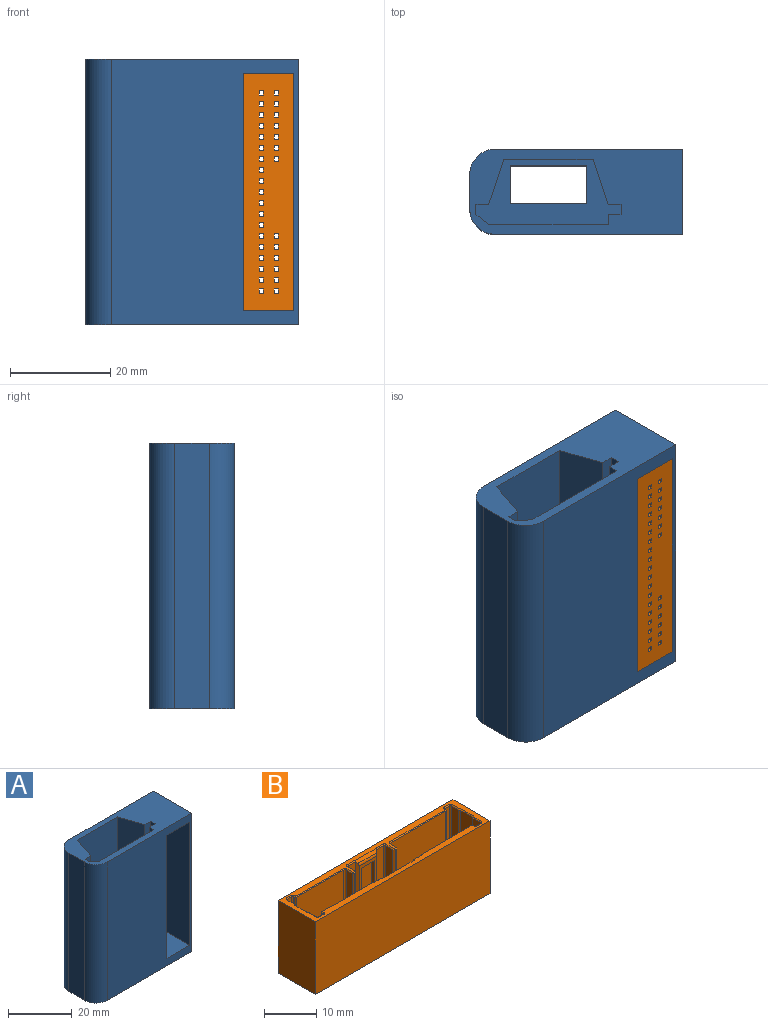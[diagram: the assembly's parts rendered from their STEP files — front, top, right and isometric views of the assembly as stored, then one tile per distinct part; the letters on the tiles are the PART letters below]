
ASSEMBLY  parts=2 mates=1
PART A: 28 faces, bbox 42.5x17x53 mm
  f0: plane 42.5x17mm, normal (0,0,-1), area 597.1mm2, adj f2,f3,f4,f5,f22,f23,f24,f25
  f1: plane 29x13.02mm, normal (0,0,1), area 182.2mm2, adj f11,f12,f13,f14,f15,f16,f17,f18
  f2: plane 53x37.42mm, normal (0,-1,0), area 1511.3mm2, adj f0,f5,f6,f7,f8,f9,f10,f26
  f3: plane 53x37.42mm, normal (0,1,0), area 1511.3mm2, adj f0,f5,f6,f7,f8,f9,f10,f27
  f4: plane 53x6.84mm, normal (-1,0,0), area 362.5mm2, adj f0,f6,f26,f27
  f5: plane 53x17mm, normal (1,0,0), area 901mm2, adj f0,f2,f3,f6
  f6: plane 42.5x17mm, normal (0,0,1), area 414.9mm2, adj f2,f3,f4,f5,f11,f12,f13,f14
  f7: plane 17x10mm, normal (0,0,-1), area 170mm2, adj f2,f3,f8,f10
  f8: plane 47.2x17mm, normal (-1,0,0), area 802.4mm2, adj f2,f3,f7,f9
  f9: plane 17x10mm, normal (0,0,1), area 170mm2, adj f2,f3,f8,f10
  f10: plane 47.2x17mm, normal (1,0,0), area 802.4mm2, adj f2,f3,f7,f9
  f11: plane 51.5x2mm, normal (1,0,0), area 103mm2, adj f1,f6,f12,f21
  f12: plane 51.5x2.54mm, normal (0.62,0.79,0), area 166.5mm2, adj f1,f6,f11,f13
  f13: plane 51.5x23.92mm, normal (0,1,0), area 1231.9mm2, adj f1,f6,f12,f14
  f14: plane 51.5x2mm, normal (-1,0,0), area 103mm2, adj f1,f6,f13,f15
  f15: plane 51.5x2.54mm, normal (0,1,0), area 130.8mm2, adj f1,f6,f14,f16
  f16: plane 51.5x2mm, normal (-1,0,0), area 103mm2, adj f1,f6,f15,f17
  f17: plane 51.5x2.54mm, normal (0,-1,0), area 130.8mm2, adj f1,f6,f16,f18
  f18: plane 51.5x9.02mm, normal (-0.95,-0.32,0), area 490.5mm2, adj f1,f6,f17,f19
  f19: plane 51.5x17.8mm, normal (0,-1,0), area 916.7mm2, adj f1,f6,f18,f20
  f20: plane 51.5x9.02mm, normal (0.95,-0.32,0), area 490.5mm2, adj f1,f6,f19,f21
  f21: plane 51.5x2.54mm, normal (0,-1,0), area 130.8mm2, adj f1,f6,f11,f20
  f22: plane 15.25x1.5mm, normal (0,-1,0), area 22.9mm2, adj f0,f1,f23,f25
  f23: plane 7.5x1.5mm, normal (1,0,0), area 11.3mm2, adj f0,f1,f22,f24
  f24: plane 15.25x1.5mm, normal (0,1,0), area 22.9mm2, adj f0,f1,f23,f25
  f25: plane 7.5x1.5mm, normal (-1,0,0), area 11.3mm2, adj f0,f1,f22,f24
  f26: cylinder r=5.08mm len=53mm, axis (0,0,-1), area 422.9mm2, adj f0,f2,f4,f6
  f27: cylinder r=5.08mm len=53mm, axis (0,0,1), area 422.9mm2, adj f0,f3,f4,f6
PART B: 258 faces, bbox 47.3x10.1x17.1 mm
  f0: plane 47.2x10mm, normal (0,0,-1), area 448.9mm2, adj f3,f4,f128,f129,f130,f131,f132,f133
  f1: plane 44.6x8.4mm, normal (0,0,1), area 288.9mm2, adj f9,f10,f22,f23,f34,f35,f39,f40
  f2: plane 47.2x10mm, normal (0,0,1), area 137.9mm2, adj f3,f4,f5,f6,f7,f8,f11,f12
  f3: plane 47.2x17mm, normal (0,-1,0), area 802.4mm2, adj f0,f2,f4,f128
  f4: plane 17x10mm, normal (1,0,0), area 170mm2, adj f0,f2,f3,f129
  f5: plane 2x0.2mm, normal (0,-0.71,0.71), area 0.5mm2, adj f2,f6,f81,f82
  f6: cone r=0.3mm half-angle=45deg, axis (0,0,1), area 0.1mm2, adj f2,f5,f7,f83
  f7: plane 2.1x0.2mm, normal (-0.71,0,0.71), area 0.6mm2, adj f2,f6,f8,f84
  f8: plane 0.38x0.38mm, normal (-0.5,-0.5,0.71), area 0.1mm2, adj f2,f7,f9,f11
  f9: plane 13.8x0.3mm, normal (-0.71,-0.71,0), area 5.9mm2, adj f1,f8,f10,f84
  f10: plane 13.8x0.4mm, normal (0,-1,0), area 5.5mm2, adj f1,f9,f11,f93
  f11: plane 0.4x0.2mm, normal (0,-0.71,0.71), area 0.1mm2, adj f2,f8,f10,f12
  f12: plane 0.38x0.38mm, normal (0.5,-0.5,0.71), area 0.1mm2, adj f2,f11,f13,f93
  f13: plane 1.6x0.2mm, normal (0.71,0,0.71), area 0.4mm2, adj f2,f12,f14,f94
  f14: cone r=0.4mm half-angle=45deg, axis (0,0,1), area 0.2mm2, adj f2,f13,f15,f95
  f15: plane 14.9x0.2mm, normal (0,-0.71,0.71), area 4.2mm2, adj f2,f14,f16,f96
  f16: cone r=0.2mm half-angle=45deg, axis (0,0,-1), area 0.1mm2, adj f2,f15,f17,f97
  f17: plane 0.2x0.2mm, normal (0.71,0,0.71), area 0.1mm2, adj f2,f16,f18,f98
  f18: cone r=0.4mm half-angle=45deg, axis (0,0,1), area 0.2mm2, adj f2,f17,f19,f99
  f19: plane 1.1x0.2mm, normal (0,-0.71,0.71), area 0.3mm2, adj f2,f18,f20,f100
  f20: cone r=0.4mm half-angle=45deg, axis (0,0,1), area 0.2mm2, adj f2,f19,f21,f101
  f21: plane 2x0.2mm, normal (-0.71,0,0.71), area 0.6mm2, adj f2,f20,f22,f24
  f22: plane 13.8x2mm, normal (-1,0,0), area 27.6mm2, adj f1,f21,f23,f101
  f23: plane 13.8x0.35mm, normal (-0.87,-0.5,0), area 5.5mm2, adj f1,f22,f24,f102
  f24: plane 0.4x0.4mm, normal (-0.61,-0.35,0.71), area 0.1mm2, adj f2,f21,f23,f25
  f25: plane 3.21x0.2mm, normal (-0.71,0,0.71), area 0.9mm2, adj f2,f24,f26,f102
  f26: plane 0.4x0.4mm, normal (-0.61,0.35,0.71), area 0.1mm2, adj f2,f25,f27,f103
  f27: plane 2x0.2mm, normal (-0.71,0,0.71), area 0.6mm2, adj f2,f26,f28,f104
  f28: cone r=0.4mm half-angle=45deg, axis (0,0,1), area 0.2mm2, adj f2,f27,f29,f105
  f29: plane 1.1x0.2mm, normal (0,0.71,0.71), area 0.3mm2, adj f2,f28,f30,f106
  f30: cone r=0.4mm half-angle=45deg, axis (0,0,1), area 0.2mm2, adj f2,f29,f31,f107
  f31: plane 0.2x0.2mm, normal (0.71,0,0.71), area 0.1mm2, adj f2,f30,f32,f108
  f32: cone r=0.2mm half-angle=45deg, axis (0,0,-1), area 0.1mm2, adj f2,f31,f33,f109
  f33: plane 13.5x0.2mm, normal (0,0.71,0.71), area 3.8mm2, adj f2,f32,f34,f36
  f34: plane 13.8x13.5mm, normal (0,1,0), area 186.3mm2, adj f1,f33,f35,f109
  f35: plane 13.8x0.35mm, normal (-0.5,0.87,0), area 5.5mm2, adj f1,f34,f36,f110
  f36: plane 0.4x0.4mm, normal (-0.35,0.61,0.71), area 0.1mm2, adj f2,f33,f35,f37
  f37: plane 1.91x0.2mm, normal (0,0.71,0.71), area 0.5mm2, adj f2,f36,f38,f110
  f38: plane 0.4x0.4mm, normal (-0.35,0.61,0.71), area 0.1mm2, adj f2,f37,f39,f41
  f39: plane 13.8x0.35mm, normal (-0.5,0.87,0), area 5.5mm2, adj f1,f38,f40,f110
  f40: plane 13.8x8.11mm, normal (0,1,0), area 111.9mm2, adj f1,f39,f41,f111
  f41: plane 8.21x0.2mm, normal (0,0.71,0.71), area 2.3mm2, adj f2,f38,f40,f42
  f42: plane 0.4x0.4mm, normal (0.35,0.61,0.71), area 0.1mm2, adj f2,f41,f43,f111
  f43: plane 1.91x0.2mm, normal (0,0.71,0.71), area 0.5mm2, adj f2,f42,f44,f112
  f44: plane 0.4x0.4mm, normal (0.35,0.61,0.71), area 0.1mm2, adj f2,f43,f45,f47
  f45: plane 13.8x0.35mm, normal (0.5,0.87,0), area 5.5mm2, adj f1,f44,f46,f112
  f46: plane 13.8x13.5mm, normal (0,1,0), area 186.3mm2, adj f1,f45,f47,f113
  f47: plane 13.5x0.2mm, normal (0,0.71,0.71), area 3.8mm2, adj f2,f44,f46,f48
  f48: cone r=0.2mm half-angle=45deg, axis (0,0,-1), area 0.1mm2, adj f2,f47,f49,f113
  f49: plane 0.2x0.2mm, normal (-0.71,0,0.71), area 0.1mm2, adj f2,f48,f50,f114
  f50: cone r=0.4mm half-angle=45deg, axis (0,0,1), area 0.2mm2, adj f2,f49,f51,f115
  f51: plane 1.1x0.2mm, normal (0,0.71,0.71), area 0.3mm2, adj f2,f50,f52,f116
  f52: cone r=0.4mm half-angle=45deg, axis (0,0,1), area 0.2mm2, adj f2,f51,f53,f117
  f53: plane 2x0.2mm, normal (0.71,0,0.71), area 0.6mm2, adj f2,f52,f54,f56
  f54: plane 13.8x2mm, normal (1,0,0), area 27.6mm2, adj f1,f53,f55,f117
  f55: plane 13.8x0.35mm, normal (0.87,0.5,0), area 5.5mm2, adj f1,f54,f56,f118
  f56: plane 0.4x0.4mm, normal (0.61,0.35,0.71), area 0.1mm2, adj f2,f53,f55,f57
  f57: plane 3.21x0.2mm, normal (0.71,0,0.71), area 0.9mm2, adj f2,f56,f58,f118
  f58: plane 0.4x0.4mm, normal (0.61,-0.35,0.71), area 0.1mm2, adj f2,f57,f59,f119
  f59: plane 2x0.2mm, normal (0.71,0,0.71), area 0.6mm2, adj f2,f58,f60,f120
  f60: cone r=0.4mm half-angle=45deg, axis (0,0,1), area 0.2mm2, adj f2,f59,f61,f121
  f61: plane 1.1x0.2mm, normal (0,-0.71,0.71), area 0.3mm2, adj f2,f60,f62,f122
  f62: cone r=0.4mm half-angle=45deg, axis (0,0,1), area 0.2mm2, adj f2,f61,f63,f123
  f63: plane 0.2x0.2mm, normal (-0.71,0,0.71), area 0.1mm2, adj f2,f62,f64,f124
  f64: cone r=0.2mm half-angle=45deg, axis (0,0,-1), area 0.1mm2, adj f2,f63,f65,f125
  f65: plane 12.7x0.2mm, normal (0,-0.71,0.71), area 3.6mm2, adj f2,f64,f66,f126
  f66: cone r=0.4mm half-angle=45deg, axis (0,0,1), area 0.2mm2, adj f2,f65,f67,f127
  f67: plane 1.6x0.2mm, normal (-0.71,0,0.71), area 0.4mm2, adj f2,f66,f68,f70
  f68: plane 13.8x1.6mm, normal (-1,0,0), area 22.1mm2, adj f1,f67,f69,f127
  f69: plane 13.8x0.3mm, normal (-0.71,-0.71,0), area 5.9mm2, adj f1,f68,f70,f72
  f70: plane 0.38x0.38mm, normal (-0.5,-0.5,0.71), area 0.1mm2, adj f2,f67,f69,f71
  f71: plane 0.4x0.2mm, normal (0,-0.71,0.71), area 0.1mm2, adj f2,f70,f72,f74
  f72: plane 13.8x0.4mm, normal (0,-1,0), area 5.5mm2, adj f1,f69,f71,f73
  f73: plane 13.8x0.3mm, normal (0.71,-0.71,0), area 5.9mm2, adj f1,f72,f74,f86
  f74: plane 0.38x0.38mm, normal (0.5,-0.5,0.71), area 0.1mm2, adj f2,f71,f73,f75
  f75: plane 2.1x0.2mm, normal (0.71,0,0.71), area 0.6mm2, adj f2,f74,f76,f86
  f76: cone r=0.3mm half-angle=45deg, axis (0,0,1), area 0.1mm2, adj f2,f75,f77,f85
  f77: plane 2x0.2mm, normal (0,-0.71,0.71), area 0.5mm2, adj f2,f76,f78,f79
  f78: plane 13.8x2mm, normal (0,-1,0), area 27.6mm2, adj f1,f77,f79,f85
  f79: plane 14.09x0.79mm, normal (-0.71,-0.71,0), area 9.5mm2, adj f1,f2,f77,f78,f80,f87,f92
  f80: plane 5.86x0.64mm, normal (0,-0.82,0.57), area 4.2mm2, adj f2,f79,f81,f92
  f81: plane 14.09x0.79mm, normal (0.71,-0.71,0), area 9.5mm2, adj f1,f2,f5,f80,f82,f87,f92
  f82: plane 13.8x2mm, normal (0,-1,0), area 27.6mm2, adj f1,f5,f81,f83
  f83: cylinder r=0.2mm len=13.8mm, axis (0,0,-1), area 4.3mm2, adj f1,f6,f82,f84
  f84: plane 13.8x2.1mm, normal (-1,0,0), area 29mm2, adj f1,f7,f9,f83
  f85: cylinder r=0.2mm len=13.8mm, axis (0,0,-1), area 4.3mm2, adj f1,f76,f78,f86
  f86: plane 13.8x2.1mm, normal (1,0,0), area 29mm2, adj f1,f73,f75,f85
  f87: plane 12.78x4.6mm, normal (0,-1,0), area 15.6mm2, adj f1,f79,f81,f88,f90,f91,f92
  f88: plane 12.13x0.9mm, normal (-1,0,0), area 10.9mm2, adj f1,f87,f89,f91
  f89: plane 12.13x3.6mm, normal (0,-1,0), area 43.7mm2, adj f1,f88,f90,f91
  f90: plane 12.13x0.9mm, normal (1,0,0), area 10.9mm2, adj f1,f87,f89,f91
  f91: plane 3.6x0.9mm, normal (0,0.14,-0.99), area 3.3mm2, adj f87,f88,f89,f90
  f92: cylinder r=1mm len=4.96mm, axis (1,0,0), area 2.9mm2, adj f79,f80,f81,f87
  f93: plane 13.8x0.3mm, normal (0.71,-0.71,0), area 5.9mm2, adj f1,f10,f12,f94
  f94: plane 13.8x1.6mm, normal (1,0,0), area 22.1mm2, adj f1,f13,f93,f95
  f95: cylinder r=0.3mm len=13.8mm, axis (0,0,1), area 6.5mm2, adj f1,f14,f94,f96
  f96: plane 14.9x13.8mm, normal (0,-1,0), area 205.6mm2, adj f1,f15,f95,f97
  f97: cylinder r=0.3mm len=13.8mm, axis (0,0,1), area 6.5mm2, adj f1,f16,f96,f98
  f98: plane 13.8x0.2mm, normal (1,0,0), area 2.8mm2, adj f1,f17,f97,f99
  f99: cylinder r=0.3mm len=13.8mm, axis (0,0,1), area 6.5mm2, adj f1,f18,f98,f100
  f100: plane 13.8x1.1mm, normal (0,-1,0), area 15.2mm2, adj f1,f19,f99,f101
  f101: cylinder r=0.3mm len=13.8mm, axis (0,0,1), area 6.5mm2, adj f1,f20,f22,f100
  f102: plane 13.8x3.11mm, normal (-1,0,0), area 42.9mm2, adj f1,f23,f25,f103
  f103: plane 13.8x0.35mm, normal (-0.87,0.5,0), area 5.5mm2, adj f1,f26,f102,f104
  f104: plane 13.8x2mm, normal (-1,0,0), area 27.6mm2, adj f1,f27,f103,f105
  f105: cylinder r=0.3mm len=13.8mm, axis (0,0,1), area 6.5mm2, adj f1,f28,f104,f106
  f106: plane 13.8x1.1mm, normal (0,1,0), area 15.2mm2, adj f1,f29,f105,f107
  f107: cylinder r=0.3mm len=13.8mm, axis (0,0,1), area 6.5mm2, adj f1,f30,f106,f108
  f108: plane 13.8x0.2mm, normal (1,0,0), area 2.8mm2, adj f1,f31,f107,f109
  f109: cylinder r=0.3mm len=13.8mm, axis (0,0,1), area 6.5mm2, adj f1,f32,f34,f108
  f110: plane 13.8x1.85mm, normal (0,1,0), area 25.6mm2, adj f1,f35,f37,f39
  f111: plane 13.8x0.35mm, normal (0.5,0.87,0), area 5.5mm2, adj f1,f40,f42,f112
  f112: plane 13.8x1.85mm, normal (0,1,0), area 25.6mm2, adj f1,f43,f45,f111
  f113: cylinder r=0.3mm len=13.8mm, axis (0,0,1), area 6.5mm2, adj f1,f46,f48,f114
  f114: plane 13.8x0.2mm, normal (-1,0,0), area 2.8mm2, adj f1,f49,f113,f115
  f115: cylinder r=0.3mm len=13.8mm, axis (0,0,1), area 6.5mm2, adj f1,f50,f114,f116
  f116: plane 13.8x1.1mm, normal (0,1,0), area 15.2mm2, adj f1,f51,f115,f117
  f117: cylinder r=0.3mm len=13.8mm, axis (0,0,1), area 6.5mm2, adj f1,f52,f54,f116
  f118: plane 13.8x3.11mm, normal (1,0,0), area 42.9mm2, adj f1,f55,f57,f119
  f119: plane 13.8x0.35mm, normal (0.87,-0.5,0), area 5.5mm2, adj f1,f58,f118,f120
  f120: plane 13.8x2mm, normal (1,0,0), area 27.6mm2, adj f1,f59,f119,f121
  f121: cylinder r=0.3mm len=13.8mm, axis (0,0,1), area 6.5mm2, adj f1,f60,f120,f122
  f122: plane 13.8x1.1mm, normal (0,-1,0), area 15.2mm2, adj f1,f61,f121,f123
  f123: cylinder r=0.3mm len=13.8mm, axis (0,0,1), area 6.5mm2, adj f1,f62,f122,f124
  f124: plane 13.8x0.2mm, normal (-1,0,0), area 2.8mm2, adj f1,f63,f123,f125
  f125: cylinder r=0.3mm len=13.8mm, axis (0,0,1), area 6.5mm2, adj f1,f64,f124,f126
  f126: plane 13.8x12.7mm, normal (0,-1,0), area 175.3mm2, adj f1,f65,f125,f127
  f127: cylinder r=0.3mm len=13.8mm, axis (0,0,1), area 6.5mm2, adj f1,f66,f68,f126
  f128: plane 17x10mm, normal (-1,0,0), area 170mm2, adj f0,f2,f3,f129
  f129: plane 47.2x17mm, normal (0,1,0), area 802.4mm2, adj f0,f2,f4,f128
  f130: plane 3x0.85mm, normal (0,-1,0), area 2.6mm2, adj f0,f1,f131,f133
  f131: plane 3x0.85mm, normal (-1,0,0), area 2.6mm2, adj f0,f1,f130,f132
  f132: plane 3x0.85mm, normal (0,1,0), area 2.6mm2, adj f0,f1,f131,f133
  f133: plane 3x0.85mm, normal (1,0,0), area 2.6mm2, adj f0,f1,f130,f132
  f134: plane 3x0.85mm, normal (0,1,0), area 2.6mm2, adj f0,f1,f135,f137
  f135: plane 3x0.85mm, normal (1,0,0), area 2.6mm2, adj f0,f1,f134,f136
  f136: plane 3x0.85mm, normal (0,-1,0), area 2.6mm2, adj f0,f1,f135,f137
  f137: plane 3x0.85mm, normal (-1,0,0), area 2.6mm2, adj f0,f1,f134,f136
  f138: plane 3x0.85mm, normal (0,-1,0), area 2.6mm2, adj f0,f1,f139,f141
  f139: plane 3x0.85mm, normal (-1,0,0), area 2.6mm2, adj f0,f1,f138,f140
  f140: plane 3x0.85mm, normal (0,1,0), area 2.6mm2, adj f0,f1,f139,f141
  f141: plane 3x0.85mm, normal (1,0,0), area 2.6mm2, adj f0,f1,f138,f140
  f142: plane 3x0.85mm, normal (0,-1,0), area 2.5mm2, adj f0,f1,f143,f145
  f143: plane 3x0.85mm, normal (-1,0,0), area 2.6mm2, adj f0,f1,f142,f144
  f144: plane 3x0.85mm, normal (0,1,0), area 2.5mm2, adj f0,f1,f143,f145
  f145: plane 3x0.85mm, normal (1,0,0), area 2.6mm2, adj f0,f1,f142,f144
  f146: plane 3x0.85mm, normal (0,-1,0), area 2.6mm2, adj f0,f1,f147,f149
  f147: plane 3x0.85mm, normal (-1,0,0), area 2.6mm2, adj f0,f1,f146,f148
  f148: plane 3x0.85mm, normal (0,1,0), area 2.6mm2, adj f0,f1,f147,f149
  f149: plane 3x0.85mm, normal (1,0,0), area 2.6mm2, adj f0,f1,f146,f148
  f150: plane 3x0.85mm, normal (0,-1,0), area 2.6mm2, adj f0,f1,f151,f153
  f151: plane 3x0.85mm, normal (-1,0,0), area 2.6mm2, adj f0,f1,f150,f152
  f152: plane 3x0.85mm, normal (0,1,0), area 2.6mm2, adj f0,f1,f151,f153
  f153: plane 3x0.85mm, normal (1,0,0), area 2.6mm2, adj f0,f1,f150,f152
  f154: plane 3x0.85mm, normal (0,-1,0), area 2.6mm2, adj f0,f1,f155,f157
  f155: plane 3x0.85mm, normal (-1,0,0), area 2.6mm2, adj f0,f1,f154,f156
  f156: plane 3x0.85mm, normal (0,1,0), area 2.6mm2, adj f0,f1,f155,f157
  f157: plane 3x0.85mm, normal (1,0,0), area 2.6mm2, adj f0,f1,f154,f156
  f158: plane 3x0.85mm, normal (0,-1,0), area 2.6mm2, adj f0,f1,f159,f161
  f159: plane 3x0.85mm, normal (-1,0,0), area 2.6mm2, adj f0,f1,f158,f160
  f160: plane 3x0.85mm, normal (0,1,0), area 2.6mm2, adj f0,f1,f159,f161
  f161: plane 3x0.85mm, normal (1,0,0), area 2.6mm2, adj f0,f1,f158,f160
  f162: plane 3x0.85mm, normal (0,-1,0), area 2.6mm2, adj f0,f1,f163,f165
  f163: plane 3x0.85mm, normal (-1,0,0), area 2.6mm2, adj f0,f1,f162,f164
  f164: plane 3x0.85mm, normal (0,1,0), area 2.6mm2, adj f0,f1,f163,f165
  f165: plane 3x0.85mm, normal (1,0,0), area 2.6mm2, adj f0,f1,f162,f164
  f166: plane 3x0.85mm, normal (0,-1,0), area 2.6mm2, adj f0,f1,f167,f169
  f167: plane 3x0.85mm, normal (-1,0,0), area 2.6mm2, adj f0,f1,f166,f168
  f168: plane 3x0.85mm, normal (0,1,0), area 2.6mm2, adj f0,f1,f167,f169
  f169: plane 3x0.85mm, normal (1,0,0), area 2.6mm2, adj f0,f1,f166,f168
  f170: plane 3x0.85mm, normal (0,-1,0), area 2.6mm2, adj f0,f1,f171,f173
  f171: plane 3x0.85mm, normal (-1,0,0), area 2.6mm2, adj f0,f1,f170,f172
  f172: plane 3x0.85mm, normal (0,1,0), area 2.6mm2, adj f0,f1,f171,f173
  f173: plane 3x0.85mm, normal (1,0,0), area 2.6mm2, adj f0,f1,f170,f172
  f174: plane 3x0.85mm, normal (0,-1,0), area 2.6mm2, adj f0,f1,f175,f177
  f175: plane 3x0.85mm, normal (-1,0,0), area 2.6mm2, adj f0,f1,f174,f176
  f176: plane 3x0.85mm, normal (0,1,0), area 2.6mm2, adj f0,f1,f175,f177
  f177: plane 3x0.85mm, normal (1,0,0), area 2.6mm2, adj f0,f1,f174,f176
  f178: plane 3x0.85mm, normal (0,-1,0), area 2.6mm2, adj f0,f1,f179,f181
  f179: plane 3x0.85mm, normal (-1,0,0), area 2.6mm2, adj f0,f1,f178,f180
  f180: plane 3x0.85mm, normal (0,1,0), area 2.6mm2, adj f0,f1,f179,f181
  f181: plane 3x0.85mm, normal (1,0,0), area 2.6mm2, adj f0,f1,f178,f180
  f182: plane 3x0.85mm, normal (0,-1,0), area 2.6mm2, adj f0,f1,f183,f185
  f183: plane 3x0.85mm, normal (-1,0,0), area 2.6mm2, adj f0,f1,f182,f184
  f184: plane 3x0.85mm, normal (0,1,0), area 2.6mm2, adj f0,f1,f183,f185
  f185: plane 3x0.85mm, normal (1,0,0), area 2.6mm2, adj f0,f1,f182,f184
  f186: plane 3x0.85mm, normal (0,-1,0), area 2.6mm2, adj f0,f1,f187,f189
  f187: plane 3x0.85mm, normal (-1,0,0), area 2.6mm2, adj f0,f1,f186,f188
  f188: plane 3x0.85mm, normal (0,1,0), area 2.6mm2, adj f0,f1,f187,f189
  f189: plane 3x0.85mm, normal (1,0,0), area 2.6mm2, adj f0,f1,f186,f188
  f190: plane 3x0.85mm, normal (0,-1,0), area 2.6mm2, adj f0,f1,f191,f193
  f191: plane 3x0.85mm, normal (-1,0,0), area 2.6mm2, adj f0,f1,f190,f192
  f192: plane 3x0.85mm, normal (0,1,0), area 2.6mm2, adj f0,f1,f191,f193
  f193: plane 3x0.85mm, normal (1,0,0), area 2.6mm2, adj f0,f1,f190,f192
  f194: plane 3x0.85mm, normal (0,-1,0), area 2.6mm2, adj f0,f1,f195,f197
  f195: plane 3x0.85mm, normal (-1,0,0), area 2.6mm2, adj f0,f1,f194,f196
  f196: plane 3x0.85mm, normal (0,1,0), area 2.6mm2, adj f0,f1,f195,f197
  f197: plane 3x0.85mm, normal (1,0,0), area 2.6mm2, adj f0,f1,f194,f196
  f198: plane 3x0.85mm, normal (0,-1,0), area 2.5mm2, adj f0,f1,f199,f201
  f199: plane 3x0.85mm, normal (-1,0,0), area 2.6mm2, adj f0,f1,f198,f200
  f200: plane 3x0.85mm, normal (0,1,0), area 2.5mm2, adj f0,f1,f199,f201
  f201: plane 3x0.85mm, normal (1,0,0), area 2.6mm2, adj f0,f1,f198,f200
  f202: plane 3x0.85mm, normal (0,-1,0), area 2.6mm2, adj f0,f1,f203,f205
  f203: plane 3x0.85mm, normal (-1,0,0), area 2.6mm2, adj f0,f1,f202,f204
  f204: plane 3x0.85mm, normal (0,1,0), area 2.6mm2, adj f0,f1,f203,f205
  f205: plane 3x0.85mm, normal (1,0,0), area 2.6mm2, adj f0,f1,f202,f204
  f206: plane 3x0.85mm, normal (0,-1,0), area 2.6mm2, adj f0,f1,f207,f209
  f207: plane 3x0.85mm, normal (-1,0,0), area 2.6mm2, adj f0,f1,f206,f208
  f208: plane 3x0.85mm, normal (0,1,0), area 2.6mm2, adj f0,f1,f207,f209
  f209: plane 3x0.85mm, normal (1,0,0), area 2.6mm2, adj f0,f1,f206,f208
  f210: plane 3x0.85mm, normal (0,-1,0), area 2.6mm2, adj f0,f1,f211,f213
  f211: plane 3x0.85mm, normal (-1,0,0), area 2.6mm2, adj f0,f1,f210,f212
  f212: plane 3x0.85mm, normal (0,1,0), area 2.6mm2, adj f0,f1,f211,f213
  f213: plane 3x0.85mm, normal (1,0,0), area 2.6mm2, adj f0,f1,f210,f212
  f214: plane 3x0.85mm, normal (0,-1,0), area 2.6mm2, adj f0,f1,f215,f217
  f215: plane 3x0.85mm, normal (-1,0,0), area 2.6mm2, adj f0,f1,f214,f216
  f216: plane 3x0.85mm, normal (0,1,0), area 2.6mm2, adj f0,f1,f215,f217
  f217: plane 3x0.85mm, normal (1,0,0), area 2.6mm2, adj f0,f1,f214,f216
  f218: plane 3x0.85mm, normal (0,-1,0), area 2.6mm2, adj f0,f1,f219,f221
  f219: plane 3x0.85mm, normal (-1,0,0), area 2.6mm2, adj f0,f1,f218,f220
  f220: plane 3x0.85mm, normal (0,1,0), area 2.6mm2, adj f0,f1,f219,f221
  f221: plane 3x0.85mm, normal (1,0,0), area 2.6mm2, adj f0,f1,f218,f220
  f222: plane 3x0.85mm, normal (0,-1,0), area 2.6mm2, adj f0,f1,f223,f225
  f223: plane 3x0.85mm, normal (-1,0,0), area 2.6mm2, adj f0,f1,f222,f224
  f224: plane 3x0.85mm, normal (0,1,0), area 2.6mm2, adj f0,f1,f223,f225
  f225: plane 3x0.85mm, normal (1,0,0), area 2.6mm2, adj f0,f1,f222,f224
  f226: plane 3x0.85mm, normal (0,-1,0), area 2.6mm2, adj f0,f1,f227,f229
  f227: plane 3x0.85mm, normal (-1,0,0), area 2.6mm2, adj f0,f1,f226,f228
  f228: plane 3x0.85mm, normal (0,1,0), area 2.6mm2, adj f0,f1,f227,f229
  f229: plane 3x0.85mm, normal (1,0,0), area 2.6mm2, adj f0,f1,f226,f228
  f230: plane 3x0.85mm, normal (0,-1,0), area 2.5mm2, adj f0,f1,f231,f233
  f231: plane 3x0.85mm, normal (-1,0,0), area 2.6mm2, adj f0,f1,f230,f232
  f232: plane 3x0.85mm, normal (0,1,0), area 2.5mm2, adj f0,f1,f231,f233
  f233: plane 3x0.85mm, normal (1,0,0), area 2.6mm2, adj f0,f1,f230,f232
  f234: plane 3x0.85mm, normal (0,-1,0), area 2.6mm2, adj f0,f1,f235,f237
  f235: plane 3x0.85mm, normal (-1,0,0), area 2.6mm2, adj f0,f1,f234,f236
  f236: plane 3x0.85mm, normal (0,1,0), area 2.6mm2, adj f0,f1,f235,f237
  f237: plane 3x0.85mm, normal (1,0,0), area 2.6mm2, adj f0,f1,f234,f236
  f238: plane 3x0.85mm, normal (0,-1,0), area 2.6mm2, adj f0,f1,f239,f241
  f239: plane 3x0.85mm, normal (-1,0,0), area 2.6mm2, adj f0,f1,f238,f240
  f240: plane 3x0.85mm, normal (0,1,0), area 2.6mm2, adj f0,f1,f239,f241
  f241: plane 3x0.85mm, normal (1,0,0), area 2.6mm2, adj f0,f1,f238,f240
  f242: plane 3x0.85mm, normal (0,-1,0), area 2.6mm2, adj f0,f1,f243,f245
  f243: plane 3x0.85mm, normal (-1,0,0), area 2.6mm2, adj f0,f1,f242,f244
  f244: plane 3x0.85mm, normal (0,1,0), area 2.6mm2, adj f0,f1,f243,f245
  f245: plane 3x0.85mm, normal (1,0,0), area 2.6mm2, adj f0,f1,f242,f244
  f246: plane 3x0.85mm, normal (0,-1,0), area 2.6mm2, adj f0,f1,f247,f249
  f247: plane 3x0.85mm, normal (-1,0,0), area 2.6mm2, adj f0,f1,f246,f248
  f248: plane 3x0.85mm, normal (0,1,0), area 2.6mm2, adj f0,f1,f247,f249
  f249: plane 3x0.85mm, normal (1,0,0), area 2.6mm2, adj f0,f1,f246,f248
  f250: plane 3x0.85mm, normal (0,-1,0), area 2.5mm2, adj f0,f1,f251,f253
  f251: plane 3x0.85mm, normal (-1,0,0), area 2.6mm2, adj f0,f1,f250,f252
  f252: plane 3x0.85mm, normal (0,1,0), area 2.5mm2, adj f0,f1,f251,f253
  f253: plane 3x0.85mm, normal (1,0,0), area 2.6mm2, adj f0,f1,f250,f252
  f254: plane 3x0.85mm, normal (0,-1,0), area 2.6mm2, adj f0,f1,f255,f257
  f255: plane 3x0.85mm, normal (-1,0,0), area 2.6mm2, adj f0,f1,f254,f256
  f256: plane 3x0.85mm, normal (0,1,0), area 2.6mm2, adj f0,f1,f255,f257
  f257: plane 3x0.85mm, normal (1,0,0), area 2.6mm2, adj f0,f1,f254,f256
PLACE A rot(axis=(-0.18,-0.06,0.98),0deg) t=(-8.54,-6.52,0.42)mm
PLACE B rot(axis=(-0.58,-0.58,-0.58),120deg) t=(11.21,1.98,26.92)mm
MATE fastened A.f10 <-> B.f3  axis (1,0,0) through (6.21,-6.52,26.92)mm
